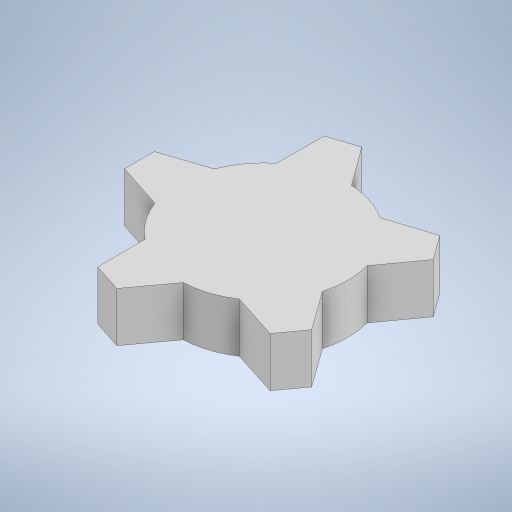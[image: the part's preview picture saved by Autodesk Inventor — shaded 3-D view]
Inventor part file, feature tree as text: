
AUTODESK INVENTOR PART (.ipt)
format: ipt  version: 2023 (Build 270158000, 158)  size: 272,896 bytes
history: native  units: in
note: dims shown in document units (in); Inventor stores cm internally (conversion verified against a paired STEP export)
features: extrude x1, sketch x1
ambient origin geometry x8: Origin, YZ Plane, XZ Plane, XY Plane, X Axis, Y Axis, Z Axis, Center Point
bodies: Solid1 (feature_tree)
feature tree (2):
  extrude  "Extrusion1"  Depth=0.1969in
  sketch  "Sketch1"  dims[d0=0.6693in d1=0.1181in d2=0.1575in d3=0.2362in d4=0.7439in d5=0.7439in d6=1.9685in d8=360.0deg d10=0.1969in d11=0.0in]
